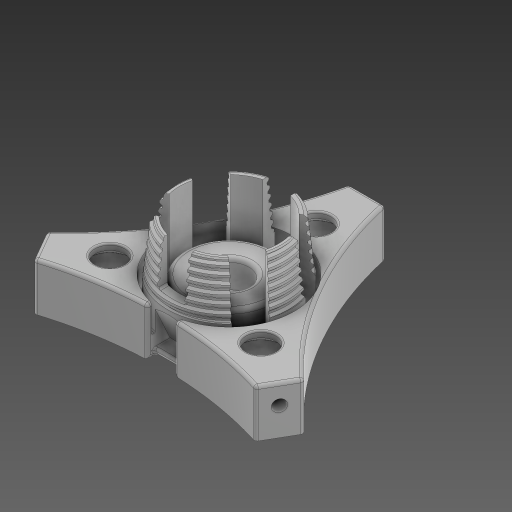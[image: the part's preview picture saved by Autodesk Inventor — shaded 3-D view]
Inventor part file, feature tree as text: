
AUTODESK INVENTOR PART (.ipt)
format: ipt  version: 2024 (Build 280153000, 153)  size: 1,678,336 bytes
history: native  units: mm
features: sketch x17, extrude x12, fillet x9, chamfer x3, hole x3, draft x2, helix x2, plane x2, pattern_circular x2, projected_geometry x2
ambient origin geometry x8: Origin, YZ Plane, XZ Plane, XY Plane, X Axis, Y Axis, Z Axis, Center Point
bodies: Solid1 (feature_tree)
feature tree (54):
  extrude  "Extrusion1"  Depth=29.5mm
  draft  "FaceDraft1"
  sketch  "Sketch2"  dims[d7=6.806784mm d8=0.55605mm]
  helix  "Coil1"  [1 undecoded]
  helix  "Coil2"  [1 undecoded]
  extrude  "Extrusion2"  Depth=0.55605mm
  extrude  "Extrusion3"  TaperAngle=0.0deg  [1 undecoded]
  fillet  "Fillet1"  [1 undecoded]
  chamfer  "Chamfer1"  Distance=0.3mm Angle=45.0deg
  plane  "Work Plane1"
  extrude  "Extrusion4"  TaperAngle=0.0deg  [1 undecoded]
  extrude  "Extrusion8"  Depth=60.0mm TaperAngle=360.0deg
  hole  "Hole2"  [1 undecoded]
  sketch  "Sketch13"  dims[d58=6.0mm d65=60.0mm d67=360.0deg]
  extrude  "Extrusion11"  Depth=10.0mm TaperAngle=0.0deg
  hole  "Bearing Hole"  [1 undecoded]
  pattern_circular  "Circular Pattern4"  Count=3 Angle=360.0deg
  extrude  "Extrusion13"  Depth=7.0mm TaperAngle=0.0deg
  sketch  "Sketch20"  dims[d126=7.504mm d127=6.0mm d128=10.679mm d129=8.89mm d130=90.0deg d131=8.0mm d132=20.594885mm d133=22.0mm d134=30.0mm d135=360.0deg]
  extrude  "Extrusion14"  Depth=1.55mm TaperAngle=45.0deg
  sketch  "Sketch18"  dims[d124=34.0mm]
  fillet  "Fillet9"  Radius=0.24mm
  chamfer  "Chamfer4"  [1 undecoded]
  chamfer  "Chamfer5"  Distance=0.5mm
  fillet  "Fillet11"  Radius=2.0mm
  draft  "FaceDraft2"
  fillet  "Fillet13"  Radius=34.767mm
  extrude  "Extrusion15"  Depth=0.5mm
  hole  "Hole5"  [1 undecoded]
  pattern_circular  "Circular Pattern5"  [2 undecoded]
  plane  "Work Plane4"
  extrude  "Extrusion16"  Depth=0.5mm
  fillet  "Fillet14"  Radius=30.0mm
  fillet  "Fillet16"  Radius=16.0mm
  extrude  "Extrusion17"  TaperAngle=0.0deg  [1 undecoded]
  extrude  "Extrusion19"  Depth=0.5mm
  fillet  "Fillet17"  Radius=0.4mm
  fillet  "Fillet18"  Radius=25.0mm
  fillet  "Fillet19"  Radius=22.0mm
  sketch  "Sketch1"  dims[d0=25.0mm d1=29.5mm d2=12.875mm d3=0.0mm d4=1.047198mm]
  projected_geometry  "Projected Loop1"
  sketch  "Sketch3"  dims[d9=6.806784mm]
  sketch  "Sketch4"  dims[d10=2.0mm d11=10.0mm d12=70.0mm d13=-1.047198mm d14=90.0deg d15=90.0deg d16=0.0mm d17=0.0mm d18=0.6mm]
  sketch  "Sketch5"  dims[d19=2.0mm d20=10.0mm d21=10.0mm d22=1.047198mm d23=90.0deg d24=90.0deg d25=0.0mm d26=0.0mm d27=0.0mm d28=0.0mm d29=0.0mm d30=0.0mm]
  sketch  "Sketch10"  dims[d31=0.6mm d32=0.3mm d33=2.0mm d34=45.0deg]
  sketch  "Sketch11"  dims[d36=-2.0mm d42=0.0mm d43=0.0mm]
  sketch  "Sketch15"  dims[d91=33.0mm d92=12.0mm d93=0.0mm]
  sketch  "Sketch17"  dims[d94=5.3mm d95=6.0mm d96=10.0mm d97=7.0mm d98=90.0deg d99=8.0mm d100=20.594885mm d122=10.0mm d123=0.0mm]
  sketch  "Sketch21"  dims[d146=11.34464mm d147=7.0mm d148=0.0mm]
  sketch  "Sketch22"  dims[d150=1.0mm d151=1.55mm d152=2.0mm d153=45.0deg]
  sketch  "Sketch25"  dims[d154=0.5mm d155=2.0mm d156=45.0deg d158=0.24mm]
  sketch  "Sketch26"  dims[d160=1.25mm d161=0.0mm d162=0.0mm]
  sketch  "Sketch28"  dims[d163=30.0deg d164=0.5mm d165=2.0mm d166=34.767mm d167=9.0mm d168=30.0deg d169=7.0mm d170=0.0mm d171=3.0mm d172=6.0mm d173=9.779mm d174=7.62mm d175=90.0deg d176=7.0mm d177=0.0mm d178=5.0mm d179=30.0mm d180=360.0deg d182=16.0mm d183=0.0mm d184=0.0mm d185=0.75mm d187=0.4mm d188=25.0mm d189=22.0mm d190=31.0mm d191=7.0mm d192=0.0mm d193=32.8mm d208=9.0mm d209=0.0mm d210=1.0mm d211=0.25mm d212=0.5mm d213=7.0mm d214=60.0mm d216=360.0deg]
  projected_geometry  "Project Cut Edges3"
note: 12 required parameter values undecoded (feature->parameter linkage not recoverable at this tier; creation-order binding heuristic only, values carry confidence <= 0.55)
